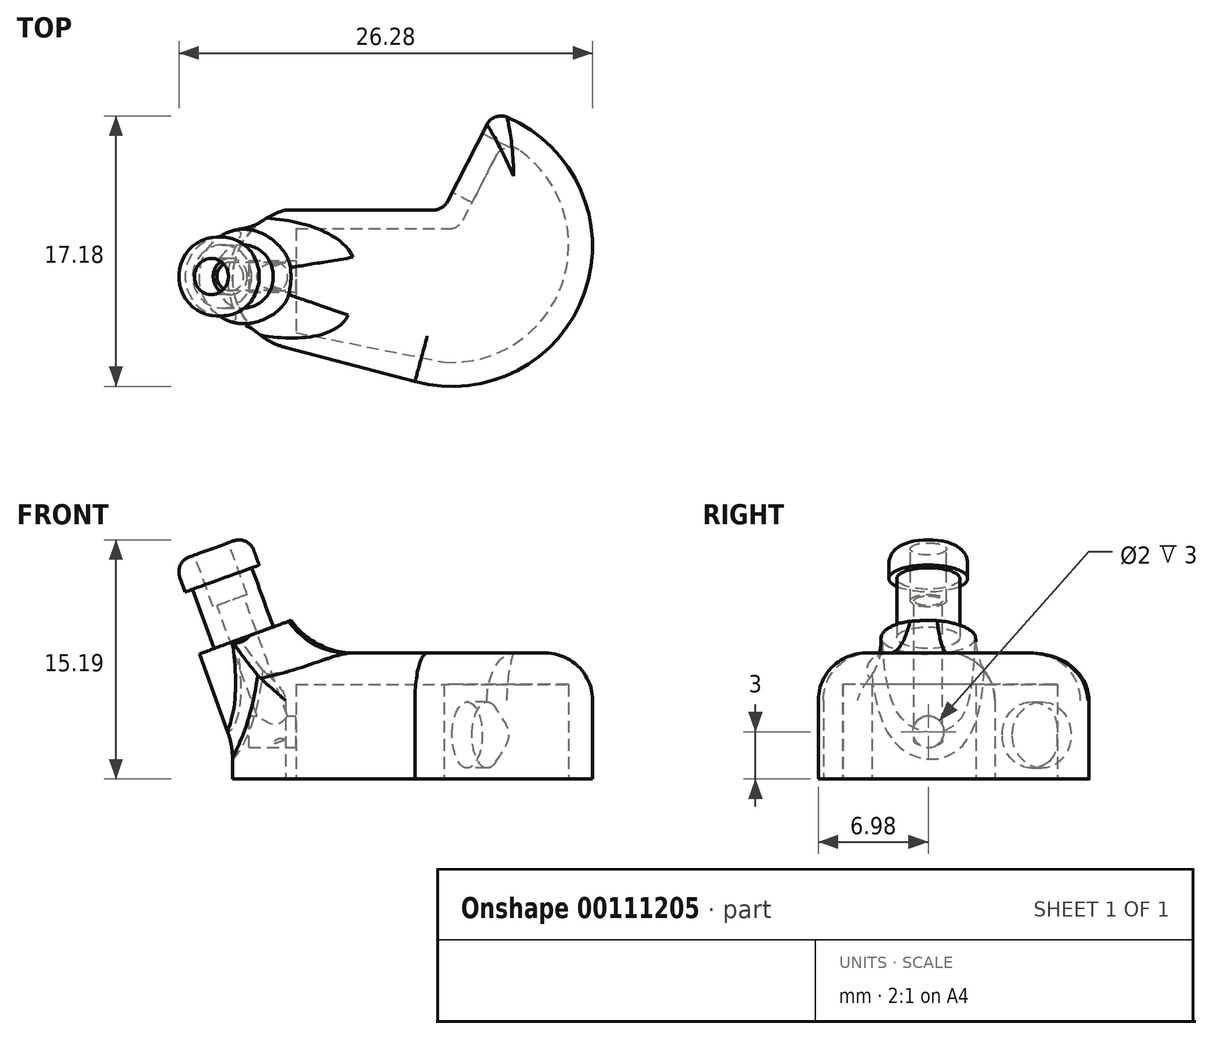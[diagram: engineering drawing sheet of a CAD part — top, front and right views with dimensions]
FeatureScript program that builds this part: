
annotation { "Feature Type Name" : "Feature", "Feature Type Description" : "" }
export const myFeature = defineFeature(function(context is Context, id is Id, definition is map)
    precondition{}
    {
        {
            var Q0;
            Q0=qCreatedBy(makeId("Top.planeOp"),FACE);
            var sketch = newSketch(context, id + "F0", { "sketchPlane" : qUnion([Q0])});
            skLineSegment(sketch, "E0", {"start": v(0, 4.22) * mm, "end": v(10, 4.22) * mm});
            skLineSegment(sketch, "E1", {"start": v(10, 4.22) * mm, "end": v(13.2, 10.44) * mm});
            skLineSegment(sketch, "E2", {"start": v(0, -4.5) * mm, "end": v(8.22, -6.66) * mm});
            skArc(sketch, "E3", {"start": v(8.22, -6.66) * mm, "mid": v(19.14, -0.56) * mm, "end": v(13.2, 10.44) * mm});
            skArc(sketch, "E4", {"start": v(0, 4.22) * mm, "mid": v(-3.37, -0.14) * mm, "end": v(0, -4.5) * mm});
            skSolve(sketch);
        }
        {
            var Q0;
            Q0=makeQuery(id+"F0.imprint","IMPRINT",FACE,{"disambiguationData":[TD([[makeQuery(id+"F0.imprint","IMPRINT",EDGE,{"derivedFrom":sQuery(id+"F0.wireOp",EDGE,"E0")}),-1.0]])]});
            extrude(context, id + "F1", {"entities" : qUnion([Q0]), "depth" : 8 * mm});
        }
        {
            var Q0;
            Q0=makeQuery(id+"F1.opExtrude","CAP_FACE",FACE,{"disambiguationData":[OSD([sQuery(id+"F0.wireOp",EDGE,"E0"),sQuery(id+"F0.wireOp",EDGE,"E1"),sQuery(id+"F0.wireOp",EDGE,"E2"),sQuery(id+"F0.wireOp",EDGE,"E3"),sQuery(id+"F0.wireOp",EDGE,"E4")])],"isStart":true});
            var sketch = newSketch(context, id + "F2", { "sketchPlane" : qUnion([Q0])});
            skLineSegment(sketch, "E5", {"start": v(0.67, -3.03) * mm, "end": v(0.67, 3.57) * mm});
            skLineSegment(sketch, "E6", {"start": v(0.67, 3.57) * mm, "end": v(10.06, 5.44) * mm});
            skLineSegment(sketch, "E7", {"start": v(0.67, -3.03) * mm, "end": v(11, -3.03) * mm});
            skLineSegment(sketch, "E8", {"start": v(11, -3.03) * mm, "end": v(13.85, -8.61) * mm});
            skArc(sketch, "E9", {"start": v(13.85, -8.61) * mm, "mid": v(17.72, -0.03) * mm, "end": v(10.06, 5.44) * mm});
            skSolve(sketch);
        }
        {
            var Q0;
            Q0=makeQuery(id+"F2.imprint","IMPRINT",FACE,{"disambiguationData":[TD([[makeQuery(id+"F2.imprint","IMPRINT",EDGE,{"derivedFrom":sQuery(id+"F2.wireOp",EDGE,"E5")}),-1.0]])]});
            extrude(context, id + "F3", {"entities" : qUnion([Q0]), "operationType" : NewBodyOperationType.REMOVE, "oppositeDirection" : true, "depth" : 6 * mm});
        }
        {
            var Q0;
            Q0=makeQuery(id+"F3.boolean.opBoolean","COPY",FACE,{"derivedFrom":makeQuery(id+"F3.opExtrude","SWEPT_FACE",FACE,{"disambiguationData":[OSD([sQuery(id+"F2.wireOp",EDGE,"E5")])]})});
            var sketch = newSketch(context, id + "F4", { "sketchPlane" : qUnion([Q0])});
            skCircle(sketch, "E10", {"center": v(0, 3) * mm, "radius": 1 * mm});
            skPoint(sketch, "E10.centerSnap0", {"position": v(3.03, 3) * mm});
            skSolve(sketch);
        }
        {
            var Q0;
            Q0=qCreatedBy(makeId("Top.planeOp"),FACE);
            var sketch = newSketch(context, id + "F5", { "sketchPlane" : qUnion([Q0])});
            skLineSegment(sketch, "E11", {"start": v(-2.42, 7.93) * mm, "end": v(-2.42, -5.03) * mm});
            skSolve(sketch);
        }
        {
            var Q0;
            Q0=makeQuery(id+"F1.opExtrude","CAP_FACE",FACE,{"disambiguationData":[OSD([sQuery(id+"F0.wireOp",EDGE,"E0"),sQuery(id+"F0.wireOp",EDGE,"E1"),sQuery(id+"F0.wireOp",EDGE,"E2"),sQuery(id+"F0.wireOp",EDGE,"E3"),sQuery(id+"F0.wireOp",EDGE,"E4")])],"isStart":true});
            var Q1;
            Q1=sQuery(id+"F5.wireOp",EDGE,"E11");
            cPlane(context, id + "F6", {"entities" : qUnion([Q0, Q1]), "cplaneType" : CPlaneType.LINE_ANGLE, "offset" : 25 * mm, "angle" : 0 * degree, "width" : 150 * mm, "height" : 150 * mm});
        }
        {
            var Q0;
            Q0=qCreatedBy(id+"F6.planeOp",FACE);
            var sketch = newSketch(context, id + "F7", { "sketchPlane" : qUnion([Q0])});
            skCircle(sketch, "E12", {"center": v(-2.08, 0) * mm, "radius": 1 * mm});
            skSolve(sketch);
        }
        {
            var Q0;
            Q0 = qSketchRegion(id + "F7", true);
            extrude(context, id + "F8", {"entities" : qUnion([Q0]), "operationType" : NewBodyOperationType.REMOVE, "endBound" : BoundingType.THROUGH_ALL, "oppositeDirection" : true, "depth" : 25 * mm});
        }
        {
            var Q0;
            {var subQ0=sQuery(id+"F0.wireOp",EDGE,"E4");var subQ1=sQuery(id+"F0.wireOp",EDGE,"E1");var subQ2=sQuery(id+"F0.wireOp",EDGE,"E0");var subQ3=sQuery(id+"F0.wireOp",EDGE,"E2");var subQ4=sQuery(id+"F0.wireOp",EDGE,"E3");Q0=makeQuery(id+"FRAegpGUTcR0WfW_1.boolean.opBoolean","SPLIT",FACE,{"disambiguationData":[TD([makeQuery(id+"F1.opExtrude","SWEPT_FACE",FACE,{"disambiguationData":[OSD([subQ2])]}),makeQuery(id+"F1.opExtrude","SWEPT_FACE",FACE,{"disambiguationData":[OSD([subQ1])]}),makeQuery(id+"F1.opExtrude","SWEPT_FACE",FACE,{"disambiguationData":[OSD([subQ3])]}),makeQuery(id+"F1.opExtrude","SWEPT_FACE",FACE,{"disambiguationData":[OSD([subQ4])]}),makeQuery(id+"F1.opExtrude","SWEPT_FACE",FACE,{"disambiguationData":[OSD([subQ0])]}),makeQuery(id+"F3.boolean.opBoolean","COPY",FACE,{"derivedFrom":makeQuery(id+"F3.opExtrude","SWEPT_FACE",FACE,{"disambiguationData":[OSD([sQuery(id+"F2.wireOp",EDGE,"E5")])]})}),makeQuery(id+"F3.boolean.opBoolean","COPY",FACE,{"derivedFrom":makeQuery(id+"F3.opExtrude","SWEPT_FACE",FACE,{"disambiguationData":[OSD([sQuery(id+"F2.wireOp",EDGE,"E6")])]})}),makeQuery(id+"F3.boolean.opBoolean","COPY",FACE,{"derivedFrom":makeQuery(id+"F3.opExtrude","SWEPT_FACE",FACE,{"disambiguationData":[OSD([sQuery(id+"F2.wireOp",EDGE,"E7")])]})}),makeQuery(id+"F3.boolean.opBoolean","COPY",FACE,{"derivedFrom":makeQuery(id+"F3.opExtrude","SWEPT_FACE",FACE,{"disambiguationData":[OSD([sQuery(id+"F2.wireOp",EDGE,"E8")])]})}),makeQuery(id+"F3.boolean.opBoolean","COPY",FACE,{"derivedFrom":makeQuery(id+"F3.opExtrude","SWEPT_FACE",FACE,{"disambiguationData":[OSD([sQuery(id+"F2.wireOp",EDGE,"E9")])]})}),makeQuery(id+"FRAegpGUTcR0WfW_1.opExtrude","SWEPT_FACE",FACE,{"disambiguationData":[OSD([sQuery(id+"F8U8vHJtzTjUuwL_1.wireOp",EDGE,"gdrP36Y7-fI1G-Q2D7-S0Vl-d63eQvXMdG0R")])]})])],"derivedFrom":makeQuery(id+"F1.opExtrude","CAP_FACE",FACE,{"disambiguationData":[OSD([subQ2,subQ1,subQ3,subQ4,subQ0])],"isStart":true})});}
            var sketch = newSketch(context, id + "F9", { "sketchPlane" : qUnion([Q0])});
            skLineSegment(sketch, "E13.bottom", {"start": v(0.67, -3.03) * mm, "end": v(3.26, -3.03) * mm});
            skLineSegment(sketch, "E13.top", {"start": v(0.67, 2.7) * mm, "end": v(3.26, 2.7) * mm});
            skLineSegment(sketch, "E13.left", {"start": v(0.67, -3.03) * mm, "end": v(0.67, 2.7) * mm});
            skLineSegment(sketch, "E13.right", {"start": v(3.26, -3.03) * mm, "end": v(3.26, 2.7) * mm});
            skSolve(sketch);
        }
        {
            var Q0;
            Q0=qCreatedBy(id+"F6.planeOp",FACE);
            cPlane(context, id + "F10", {"entities" : qUnion([Q0]), "cplaneType" : CPlaneType.OFFSET, "offset" : 8 * mm, "width" : 150 * mm, "height" : 150 * mm});
        }
        {
            var Q0;
            Q0=qCreatedBy(id+"F10.planeOp",FACE);
            var sketch = newSketch(context, id + "F11", { "sketchPlane" : qUnion([Q0])});
            skLineSegment(sketch, "E14", {"start": v(-2.42, 7.93) * mm, "end": v(-2.42, -5.03) * mm});
            skSolve(sketch);
        }
        {
            var Q0;
            Q0=makeQuery(id+"F1.opExtrude","CAP_FACE",FACE,{"disambiguationData":[OSD([sQuery(id+"F0.wireOp",EDGE,"E0"),sQuery(id+"F0.wireOp",EDGE,"E1"),sQuery(id+"F0.wireOp",EDGE,"E2"),sQuery(id+"F0.wireOp",EDGE,"E3"),sQuery(id+"F0.wireOp",EDGE,"E4")])],"isStart":false});
            var Q1;
            Q1=sQuery(id+"F11.wireOp",EDGE,"E14");
            cPlane(context, id + "F12", {"entities" : qUnion([Q0, Q1]), "cplaneType" : CPlaneType.LINE_ANGLE, "offset" : 25 * mm, "angle" : 20 * degree, "width" : 150 * mm, "height" : 150 * mm});
        }
        {
            var Q0;
            Q0=qCreatedBy(id+"F12.planeOp",FACE);
            var sketch = newSketch(context, id + "F13", { "sketchPlane" : qUnion([Q0])});
            skCircle(sketch, "E15", {"center": v(0.57, 0) * mm, "radius": 3 * mm});
            skSolve(sketch);
        }
        {
            var Q0;
            Q0 = qSketchRegion(id + "F13", true);
            extrude(context, id + "F14", {"entities" : qUnion([Q0]), "operationType" : NewBodyOperationType.ADD, "depth" : 5 * mm});
        }
        {
            var Q0;
            Q0 = qSketchRegion(id + "F13", true);
            extrude(context, id + "F15", {"entities" : qUnion([Q0]), "operationType" : NewBodyOperationType.ADD, "oppositeDirection" : true, "depth" : 1 * mm});
        }
        {
            var Q0;
            Q0=makeQuery(id+"F15.opExtrude","CAP_FACE",FACE,{"disambiguationData":[OSD([sQuery(id+"F13.wireOp",EDGE,"E15")])],"isStart":false});
            var sketch = newSketch(context, id + "F16", { "sketchPlane" : qUnion([Q0])});
            skCircle(sketch, "E16", {"center": v(0.57, 0) * mm, "radius": 2 * mm});
            skSolve(sketch);
        }
        {
            var Q0;
            Q0=makeQuery(id+"F16.imprint","IMPRINT",FACE,{"disambiguationData":[TD([[makeQuery(id+"F16.imprint","IMPRINT",EDGE,{"derivedFrom":sQuery(id+"F16.wireOp",EDGE,"E16")}),1.0]])]});
            extrude(context, id + "F17", {"entities" : qUnion([Q0]), "operationType" : NewBodyOperationType.ADD, "depth" : 4 * mm});
        }
        {
            var Q0;
            Q0=makeQuery(id+"F17.opExtrude","CAP_FACE",FACE,{"disambiguationData":[OSD([sQuery(id+"F16.wireOp",EDGE,"E16")])],"isStart":false});
            var sketch = newSketch(context, id + "F18", { "sketchPlane" : qUnion([Q0])});
            skCircle(sketch, "E17", {"center": v(0.57, 0) * mm, "radius": 2.5 * mm});
            skSolve(sketch);
        }
        {
            var Q0;
            Q0 = qSketchRegion(id + "F18", true);
            extrude(context, id + "F19", {"entities" : qUnion([Q0]), "operationType" : NewBodyOperationType.ADD, "depth" : 2 * mm});
        }
        {
            var Q0;
            Q0=makeQuery(id+"F19.opExtrude","CAP_FACE",FACE,{"disambiguationData":[OSD([sQuery(id+"F18.wireOp",EDGE,"E17")])],"isStart":false});
            var sketch = newSketch(context, id + "F20", { "sketchPlane" : qUnion([Q0])});
            skCircle(sketch, "E18", {"center": v(0.57, 0) * mm, "radius": 0.9 * mm});
            skSolve(sketch);
        }
        {
            var Q0;
            Q0 = qSketchRegion(id + "F20", true);
            extrude(context, id + "F21", {"entities" : qUnion([Q0]), "operationType" : NewBodyOperationType.REMOVE, "oppositeDirection" : true, "depth" : 13 * mm});
        }
        {
            var Q0;
            Q0=makeQuery(id+"F4.imprint","IMPRINT",FACE,{"disambiguationData":[TD([[makeQuery(id+"F4.imprint","IMPRINT",EDGE,{"derivedFrom":sQuery(id+"F4.wireOp",EDGE,"E10")}),1.0]])]});
            extrude(context, id + "F22", {"entities" : qUnion([Q0]), "operationType" : NewBodyOperationType.REMOVE, "oppositeDirection" : true, "depth" : 3 * mm});
        }
        {
            var Q0;
            Q0 = qSketchRegion(id + "F9", true);
            extrude(context, id + "F23", {"entities" : qUnion([Q0]), "operationType" : NewBodyOperationType.REMOVE, "oppositeDirection" : true, "depth" : 5 * mm});
        }
        {
            var Q0;
            Q0=makeQuery(id+"F19.opExtrude","CAP_EDGE",EDGE,{"disambiguationData":[OSD([sQuery(id+"F18.wireOp",EDGE,"E17")])],"isStart":false});
            fillet(context, id + "F24", {"entities" : qUnion([Q0]), "radius" : 1 * mm, "tangentPropagation" : true, "allowEdgeOverflow" : false});
        }
        {
            var Q0;
            Q0=makeQuery(id+"F1.opExtrude","SWEPT_EDGE",EDGE,{"disambiguationData":[OSD([sQuery(id+"F0.wireOp",EDGE,"E1"),sQuery(id+"F0.wireOp",EDGE,"E3")])]});
            var Q1;
            Q1=makeQuery(id+"F1.opExtrude","SWEPT_EDGE",EDGE,{"disambiguationData":[OSD([sQuery(id+"F0.wireOp",EDGE,"E0"),sQuery(id+"F0.wireOp",EDGE,"E1")])]});
            var Q2;
            Q2=makeQuery(id+"F3.boolean.opBoolean","COPY",EDGE,{"derivedFrom":makeQuery(id+"F3.opExtrude","SWEPT_EDGE",EDGE,{"disambiguationData":[OSD([sQuery(id+"F2.wireOp",EDGE,"E7"),sQuery(id+"F2.wireOp",EDGE,"E8")])]})});
            var Q3;
            Q3=makeQuery(id+"F3.boolean.opBoolean","COPY",EDGE,{"derivedFrom":makeQuery(id+"F3.opExtrude","SWEPT_EDGE",EDGE,{"disambiguationData":[OSD([sQuery(id+"F2.wireOp",EDGE,"E8"),sQuery(id+"F2.wireOp",EDGE,"E9")])]})});
            fillet(context, id + "F25", {"entities" : qUnion([Q0, Q1, Q2, Q3]), "radius" : 1 * mm, "tangentPropagation" : true, "allowEdgeOverflow" : false});
        }
        {
            var Q0;
            Q0=makeQuery(id+"F1.opExtrude","CAP_FACE",FACE,{"disambiguationData":[OSD([sQuery(id+"F0.wireOp",EDGE,"E0"),sQuery(id+"F0.wireOp",EDGE,"E1"),sQuery(id+"F0.wireOp",EDGE,"E2"),sQuery(id+"F0.wireOp",EDGE,"E3"),sQuery(id+"F0.wireOp",EDGE,"E4")])],"isStart":true});
            var sketch = newSketch(context, id + "F26", { "sketchPlane" : qUnion([Q0])});
            skLineSegment(sketch, "E19.bottom", {"start": v(0.67, -3.03) * mm, "end": v(2.19, -3.03) * mm});
            skLineSegment(sketch, "E19.top", {"start": v(0.67, 3.24) * mm, "end": v(2.19, 3.24) * mm});
            skLineSegment(sketch, "E19.left", {"start": v(0.67, -3.03) * mm, "end": v(0.67, 3.24) * mm});
            skLineSegment(sketch, "E19.right", {"start": v(2.19, -3.03) * mm, "end": v(2.19, 3.24) * mm});
            skSolve(sketch);
        }
        {
            var Q0;
            Q0 = qSketchRegion(id + "F26", true);
            extrude(context, id + "F27", {"entities" : qUnion([Q0]), "operationType" : NewBodyOperationType.REMOVE, "oppositeDirection" : true, "depth" : 5.5 * mm});
        }
        {
            var Q0;
            Q0=makeQuery(id+"F1.opExtrude","SWEPT_FACE",FACE,{"disambiguationData":[OSD([sQuery(id+"F0.wireOp",EDGE,"E1")])]});
            var sketch = newSketch(context, id + "F28", { "sketchPlane" : qUnion([Q0])});
            skCircle(sketch, "E20", {"center": v(-11.68, 2.8) * mm, "radius": 2.1 * mm});
            skPoint(sketch, "E20.centerSnap0", {"position": v(-11.68, 0) * mm});
            skSolve(sketch);
        }
        {
            var Q0;
            Q0=makeQuery(id+"F28.imprint","IMPRINT",FACE,{"disambiguationData":[TD([[makeQuery(id+"F28.imprint","IMPRINT",EDGE,{"derivedFrom":sQuery(id+"F28.wireOp",EDGE,"E20")}),1.0]])]});
            extrude(context, id + "F29", {"entities" : qUnion([Q0]), "operationType" : NewBodyOperationType.REMOVE, "endBound" : BoundingType.UP_TO_NEXT, "oppositeDirection" : true, "depth" : 25 * mm});
        }
        {
            var Q0;
            Q0 = qSketchRegion(id + "F26", true);
            extrude(context, id + "F30", {"entities" : qUnion([Q0]), "operationType" : NewBodyOperationType.REMOVE, "oppositeDirection" : true, "depth" : 6 * mm});
        }
        {
            var Q0;
            Q0=makeQuery(id+"F1.opExtrude","CAP_EDGE",EDGE,{"disambiguationData":[OSD([sQuery(id+"F0.wireOp",EDGE,"E0")])],"isStart":false});
            fillet(context, id + "F31", {"entities" : qUnion([Q0]), "radius" : 3 * mm, "tangentPropagation" : true, "allowEdgeOverflow" : false});
        }
        {
            var Q0;
            Q0=makeQuery(id+"F14.boolean.opBoolean","INTERSECT",EDGE,{"disambiguationData":[OD(1.0)],"derivedFrom":[makeQuery(id+"F1.opExtrude","SWEPT_FACE",FACE,{"disambiguationData":[OSD([sQuery(id+"F0.wireOp",EDGE,"E4")])]}),makeQuery(id+"F14.opExtrude","SWEPT_FACE",FACE,{"disambiguationData":[OSD([sQuery(id+"F13.wireOp",EDGE,"E15")])]})]});
            fillet(context, id + "F32", {"entities" : qUnion([Q0]), "radius" : 5 * mm, "tangentPropagation" : true, "allowEdgeOverflow" : false});
        }
        {
            var Q0;
            {var subQ0=sQuery(id+"F13.wireOp",EDGE,"E15");var subQ1=sQuery(id+"F0.wireOp",EDGE,"E4");var subQ2=sQuery(id+"F0.wireOp",EDGE,"E2");Q0=makeQuery(id+"F31.opFillet","BLEND_EDGE",EDGE,{"blendedFrom":[makeQuery(id+"F1.opExtrude","CAP_EDGE",EDGE,{"disambiguationData":[OSD([subQ2])],"isStart":false}),makeQuery(id+"F15.boolean.opBoolean","MERGE",FACE,{"derivedFrom":[makeQuery(id+"F14.boolean.opBoolean","SPLIT",FACE,{"disambiguationData":[TD([makeQuery(id+"F1.opExtrude","SWEPT_FACE",FACE,{"disambiguationData":[OSD([subQ1])]})])],"derivedFrom":makeQuery(id+"F14.opExtrude","SWEPT_FACE",FACE,{"disambiguationData":[OSD([subQ0])]})}),makeQuery(id+"F15.opExtrude","SWEPT_FACE",FACE,{"disambiguationData":[OSD([subQ0])]})]})],"blendedInto":[makeQuery(id+"F15.boolean.opBoolean","MERGE",FACE,{"derivedFrom":[makeQuery(id+"F14.boolean.opBoolean","SPLIT",FACE,{"disambiguationData":[TD([makeQuery(id+"F1.opExtrude","SWEPT_FACE",FACE,{"disambiguationData":[OSD([subQ1])]})])],"derivedFrom":makeQuery(id+"F14.opExtrude","SWEPT_FACE",FACE,{"disambiguationData":[OSD([subQ0])]})}),makeQuery(id+"F15.opExtrude","SWEPT_FACE",FACE,{"disambiguationData":[OSD([subQ0])]})]})]});}
            fillet(context, id + "F33", {"entities" : qUnion([Q0]), "radius" : 5 * mm, "tangentPropagation" : true, "allowEdgeOverflow" : false});
        }
        {
            var Q0;
            Q0=makeQuery(id+"F19.opExtrude","CAP_FACE",FACE,{"disambiguationData":[OSD([sQuery(id+"F18.wireOp",EDGE,"E17")])],"isStart":false});
            var sketch = newSketch(context, id + "F34", { "sketchPlane" : qUnion([Q0])});
            skCircle(sketch, "E21", {"center": v(0.57, 0) * mm, "radius": 1.15 * mm});
            skSolve(sketch);
        }
        {
            var Q0;
            Q0=makeQuery(id+"F34.imprint","IMPRINT",FACE,{"disambiguationData":[TD([[makeQuery(id+"F34.imprint","IMPRINT",EDGE,{"derivedFrom":sQuery(id+"F34.wireOp",EDGE,"E21")}),1.0]])]});
            var Q1;
            Q1=sQuery(id+"F34.wireOp",EDGE,"E21");
            extrude(context, id + "F35", {"entities" : qUnion([Q0]), "operationType" : NewBodyOperationType.REMOVE, "surfaceEntities" : qUnion([Q1]), "oppositeDirection" : true, "depth" : 3.5 * mm});
        }
    });
